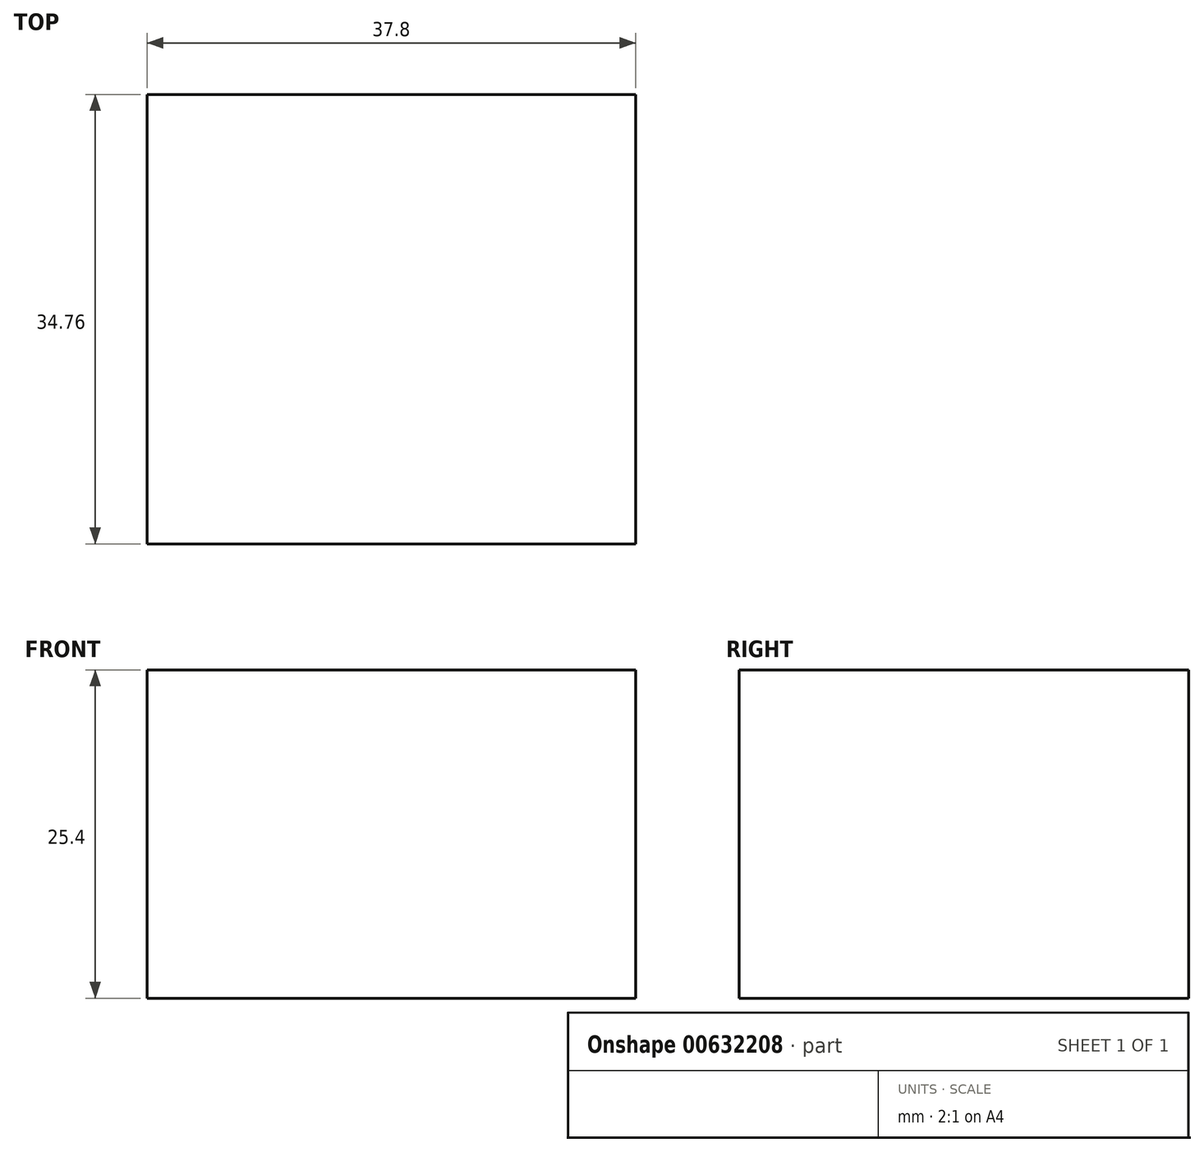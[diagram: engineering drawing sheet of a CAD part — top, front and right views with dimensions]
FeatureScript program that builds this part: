
annotation { "Feature Type Name" : "Feature", "Feature Type Description" : "" }
export const myFeature = defineFeature(function(context is Context, id is Id, definition is map)
    precondition{}
    {
        {
            var Q0;
            Q0=qCreatedBy(makeId("Top.planeOp"),FACE);
            var sketch = newSketch(context, id + "F0", { "sketchPlane" : qUnion([Q0])});
            skLineSegment(sketch, "E0.bottom", {"start": v(18.9, -17.38) * mm, "end": v(-18.9, -17.38) * mm});
            skLineSegment(sketch, "E0.top", {"start": v(18.9, 17.38) * mm, "end": v(-18.9, 17.38) * mm});
            skLineSegment(sketch, "E0.left", {"start": v(18.9, -17.38) * mm, "end": v(18.9, 17.38) * mm});
            skLineSegment(sketch, "E0.right", {"start": v(-18.9, -17.38) * mm, "end": v(-18.9, 17.38) * mm});
            skPoint(sketch, "E0.middle", {"position": v(0, 0) * mm});
            skSolve(sketch);
        }
        {
            var Q0;
            Q0=makeQuery(id+"F0.imprint","IMPRINT",FACE,{"disambiguationData":[TD([[makeQuery(id+"F0.imprint","IMPRINT",EDGE,{"derivedFrom":sQuery(id+"F0.wireOp",EDGE,"E0.bottom")}),-1.0]])]});
            extrude(context, id + "F1", {"entities" : qUnion([Q0]), "depth" : 25.4 * mm, "offsetDistance" : 25.4 * mm});
        }
    });
